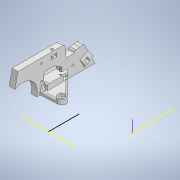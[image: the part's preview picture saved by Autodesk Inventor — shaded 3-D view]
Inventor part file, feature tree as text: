
AUTODESK INVENTOR PART (.ipt)
format: ipt  version: 2022.3 (Build 263350000, 350)  size: 2,605,056 bytes
history: native  units: mm
features: projected_geometry x116, extrude x97, sketch x67, fillet x9, reference x5, other x5, plane x4, mirror x3
ambient origin geometry x8: Origin, YZ Plane, XZ Plane, XY Plane, X Axis, Y Axis, Z Axis, Center Point
bodies: Solid1 (feature_tree)
feature tree (306):
  sketch  "Sketch1"  dims[d0=100.0mm d1=100.0mm]
  extrude  "Extrusion1"  Depth=100.0mm
  extrude  "Extrusion2"  Depth=20.0mm
  extrude  "Extrusion3"  Depth=20.0mm
  sketch  "Sketch3"  dims[d4=31.0mm d5=20.0mm]
  extrude  "Extrusion4"  Depth=19.0mm
  extrude  "Extrusion5"  Depth=10.0mm
  sketch  "Sketch4"  dims[d6=14.0mm d7=19.0mm]
  plane  "Work Plane1"
  mirror  "Mirror1"
  extrude  "Extrusion6"  Depth=2.0mm
  sketch  "Sketch8"  dims[d10=10.0mm d11=2.0mm]
  extrude  "Extrusion7"  Depth=15.0mm
  extrude  "Extrusion8"  Depth=2.0mm
  extrude  "Extrusion9"  Depth=5.0mm
  sketch  "Sketch9"  dims[d12=2.0mm d13=15.0mm]
  extrude  "Extrusion10"  Depth=2.0mm TaperAngle=0.0deg
  extrude  "Extrusion11"  TaperAngle=0.0deg  [1 undecoded]
  sketch  "Sketch10"  dims[d14=15.0mm d15=2.0mm]
  extrude  "Extrusion12"  Depth=14.0mm TaperAngle=0.0deg
  extrude  "Extrusion13"  TaperAngle=90.0deg  [1 undecoded]
  extrude  "Extrusion14"  Depth=40.0mm
  sketch  "Sketch12"  dims[d18=10.0mm d19=0.0mm d20=2.0mm d21=0.0mm]
  extrude  "Extrusion15"  Depth=15.0mm
  extrude  "Extrusion16"  Depth=5.0mm
  extrude  "Extrusion17"  Depth=13.0mm
  extrude  "Extrusion18"  Depth=8.0mm
  extrude  "Extrusion19"  Depth=18.0mm TaperAngle=0.0deg
  extrude  "Extrusion20"  Depth=49.0mm
  extrude  "Extrusion21"  Depth=5.0mm
  sketch  "Sketch15"  dims[d28=14.25mm d29=0.0mm d30=90.0deg]
  plane  "Work Plane2"
  mirror  "Mirror2"
  extrude  "Extrusion22"  TaperAngle=0.0deg  [1 undecoded]
  sketch  "Sketch17"  dims[d36=15.0mm d37=25.0mm]
  extrude  "Extrusion23"  Depth=10.0mm
  extrude  "Extrusion24"  Depth=1.6mm
  extrude  "Extrusion25"  TaperAngle=0.0deg  [1 undecoded]
  extrude  "Extrusion26"  Depth=14.0mm TaperAngle=0.0deg
  extrude  "Extrusion27"  Depth=2.0mm
  sketch  "Sketch21"  dims[d44=18.0mm d45=0.0mm d46=18.0mm d47=0.0mm]
  extrude  "Extrusion28"  Depth=2.0mm
  extrude  "Extrusion29"  Depth=6.0mm TaperAngle=0.0deg
  sketch  "Sketch22"  dims[d48=0.0mm d49=0.0mm d50=49.0mm]
  extrude  "Extrusion30"  Depth=15.0mm TaperAngle=0.0deg
  extrude  "Extrusion31"  Depth=15.0mm
  extrude  "Extrusion32"  Depth=4.0mm
  extrude  "Extrusion33"  Depth=15.0mm TaperAngle=0.0deg
  extrude  "Extrusion34"  Depth=3.0mm
  extrude  "Extrusion35"  Depth=15.0mm TaperAngle=0.0deg
  extrude  "Extrusion36"  Depth=3.2mm
  fillet  "Face Fillet1"
  fillet  "Face Fillet2"
  extrude  "Extrusion37"  Depth=3.2mm
  fillet  "Face Fillet3"
  fillet  "Face Fillet5"
  extrude  "Extrusion38"  Depth=5.0mm TaperAngle=0.0deg
  extrude  "Extrusion39"  TaperAngle=0.0deg  [1 undecoded]
  fillet  "Fillet2"  Radius=2.8mm
  extrude  "Extrusion40"  Depth=100.0mm TaperAngle=0.0deg
  sketch  "Sketch32"  dims[d76=6.0mm d77=0.0mm d78=15.0mm d79=0.0mm]
  extrude  "Extrusion41"  Depth=11.0mm
  extrude  "Extrusion42"  Depth=9.0mm TaperAngle=0.0deg
  extrude  "Extrusion43"  Depth=15.0mm
  sketch  "Sketch33"  dims[d80=15.0mm d81=0.0mm d82=3.2mm]
  extrude  "Extrusion44"  Depth=7.0mm TaperAngle=0.0deg
  extrude  "Extrusion45"  Depth=40.656mm TaperAngle=0.0deg
  extrude  "Extrusion46"  Depth=9.0mm TaperAngle=0.0deg
  extrude  "Extrusion47"  Depth=3.0mm
  sketch  "Sketch36"  dims[d91=90.0deg d92=3.0mm]
  extrude  "Extrusion48"  Depth=1.5mm TaperAngle=0.0deg
  extrude  "Extrusion49"  Depth=6.0mm
  sketch  "Sketch37"  dims[d93=3.0mm d94=15.0mm d95=0.0mm]
  extrude  "Extrusion50"  Depth=10.0mm TaperAngle=0.0deg
  extrude  "Extrusion51"  Depth=4.0mm
  extrude  "Extrusion52"  Depth=10.0mm TaperAngle=0.0deg
  extrude  "Extrusion53"  Depth=20.0mm TaperAngle=0.0deg
  sketch  "Sketch40"  dims[d100=4.0mm d101=5.0mm d102=0.0mm]
  extrude  "Extrusion54"  Depth=1.5mm
  extrude  "Extrusion55"  Depth=3.0mm
  extrude  "Extrusion56"  Depth=6.4mm
  extrude  "Extrusion57"  Depth=2.0mm
  fillet  "Fillet3"  Radius=2.0mm
  extrude  "Extrusion58"  TaperAngle=0.0deg  [1 undecoded]
  sketch  "Sketch44"  dims[d114=3.4mm d115=9.0mm d116=0.0mm]
  extrude  "Extrusion59"  TaperAngle=0.0deg  [1 undecoded]
  extrude  "Extrusion60"  Depth=10.0mm TaperAngle=0.0deg
  sketch  "Sketch45"  dims[d117=15.0mm d118=0.0mm d119=3.2mm]
  extrude  "Extrusion61"  Depth=10.0mm TaperAngle=0.0deg
  extrude  "Extrusion62"  Depth=2.0mm
  sketch  "Sketch46"  dims[d120=3.2mm d121=7.0mm d122=0.0mm]
  extrude  "Extrusion63"  Depth=6.5mm TaperAngle=0.0deg
  extrude  "Extrusion64"  Depth=17.0mm TaperAngle=0.0deg
  extrude  "Extrusion65"  Depth=3.0mm
  extrude  "Extrusion66"  Depth=5.0mm TaperAngle=0.0deg
  sketch  "Sketch49"  dims[d138=28.734mm d139=3.0mm]
  extrude  "Extrusion67"  Depth=15.0mm TaperAngle=0.0deg
  extrude  "Extrusion68"  TaperAngle=0.0deg  [1 undecoded]
  extrude  "Extrusion69"  Depth=15.0mm TaperAngle=0.0deg
  extrude  "Extrusion70"  Depth=15.0mm TaperAngle=0.0deg
  extrude  "Extrusion71"  Depth=2.0mm
  extrude  "Extrusion72"  Depth=15.0mm TaperAngle=0.0deg
  extrude  "Extrusion73"  Depth=15.0mm TaperAngle=0.0deg
  extrude  "Extrusion74"  Depth=15.0mm TaperAngle=0.0deg
  extrude  "Extrusion75"  Depth=15.0mm TaperAngle=0.0deg
  extrude  "Extrusion76"  Depth=15.0mm TaperAngle=0.0deg
  sketch  "Sketch53"  dims[d149=6.7mm d152=4.0mm]
  extrude  "Extrusion77"  Depth=15.0mm
  extrude  "Extrusion78"  Depth=15.0mm
  extrude  "Extrusion79"  Depth=2.0mm
  extrude  "Extrusion80"  Depth=15.0mm
  extrude  "Extrusion81"  TaperAngle=0.0deg  [1 undecoded]
  extrude  "Extrusion82"  Depth=15.0mm TaperAngle=0.0deg
  extrude  "Extrusion83"  Depth=15.0mm TaperAngle=0.0deg
  sketch  "Sketch59"  dims[d166=6.4mm d167=3.0mm d169=2.0mm]
  extrude  "Extrusion84"  Depth=15.0mm
  extrude  "Extrusion85"  Depth=15.0mm
  extrude  "Extrusion86"  Depth=15.0mm TaperAngle=0.0deg
  extrude  "Extrusion87"  Depth=15.0mm
  extrude  "Extrusion88"  Depth=2.0mm
  sketch  "Sketch62"  dims[d178=10.0mm d179=0.0mm d180=4.0mm d181=0.0mm]
  extrude  "Extrusion89"  Depth=15.0mm
  extrude  "Extrusion90"  Depth=15.0mm
  fillet  "Fillet4"  Radius=15.0mm
  extrude  "Extrusion91"  Depth=10.0mm TaperAngle=0.0deg
  mirror  "Mirror3"
  extrude  "Extrusion92"  Depth=10.0mm TaperAngle=0.0deg
  extrude  "Extrusion93"  Depth=15.0mm TaperAngle=0.0deg
  fillet  "Fillet5"  Radius=10.0mm
  extrude  "Extrusion94"  Depth=15.0mm TaperAngle=0.0deg
  fillet  "Fillet6"  Radius=4.0mm
  extrude  "Extrusion95"  Depth=15.0mm
  extrude  "Extrusion96"  Depth=10.0mm TaperAngle=0.0deg
  extrude  "Extrusion97"  Depth=15.0mm
  sketch  "Sketch2"  dims[d2=5.0mm d3=20.0mm]
  projected_geometry  "Projected Loop1"
  sketch  "Sketch6"  dims[d8=10.0mm d9=14.0mm]
  projected_geometry  "Projected Loop5"
  projected_geometry  "Projected Loop6"
  projected_geometry  "Projected Loop7"
  projected_geometry  "Projected Loop8"
  projected_geometry  "Projected Loop9"
  projected_geometry  "Projected Loop10"
  sketch  "Sketch11"  dims[d16=1.0mm d17=5.0mm]
  projected_geometry  "Projected Loop11"
  projected_geometry  "Projected Loop12"
  sketch  "Sketch13"  dims[d22=31.0mm d23=0.0mm d24=0.0mm]
  projected_geometry  "Projected Loop13"
  projected_geometry  "Projected Loop14"
  sketch  "Sketch14"  dims[d25=30.4mm d26=14.0mm d27=0.0mm]
  projected_geometry  "Projected Loop15"
  projected_geometry  "Projected Loop16"
  sketch  "Sketch16"  dims[d33=25.0mm d34=0.0mm d35=40.0mm]
  projected_geometry  "Projected Loop17"
  projected_geometry  "Projected Loop18"
  projected_geometry  "Projected Loop19"
  sketch  "Sketch18"  dims[d38=20.0mm d39=5.0mm]
  projected_geometry  "Projected Loop20"
  projected_geometry  "Projected Loop21"
  projected_geometry  "Projected Loop22"
  projected_geometry  "Projected Loop23"
  projected_geometry  "Projected Loop24"
  projected_geometry  "Projected Loop25"
  projected_geometry  "Projected Loop26"
  sketch  "Sketch19"  dims[d40=7.0mm d41=13.0mm]
  projected_geometry  "Projected Loop27"
  sketch  "Sketch20"  dims[d42=7.0mm d43=8.0mm]
  projected_geometry  "Projected Loop28"
  projected_geometry  "Projected Loop29"
  projected_geometry  "Projected Loop30"
  sketch  "Sketch23"  dims[d51=25.0mm d52=5.0mm]
  sketch  "Sketch24"  dims[d53=20.0mm d54=0.0mm d55=0.0mm]
  projected_geometry  "Projected Loop31"
  projected_geometry  "Projected Loop32"
  sketch  "Sketch25"  dims[d56=10.0mm d57=0.0mm d58=1.6mm]
  projected_geometry  "Projected Loop33"
  sketch  "Sketch26"  dims[d59=1.6mm d60=1.6mm]
  projected_geometry  "Projected Loop34"
  sketch  "Sketch27"  dims[d61=5.0mm d62=0.0mm d63=0.0mm d64=0.0mm]
  projected_geometry  "Projected Loop35"
  sketch  "Sketch28"  dims[d65=2.5mm d66=14.0mm d67=0.0mm]
  projected_geometry  "Projected Loop36"
  sketch  "Sketch29"  dims[d68=2.0mm d69=6.0mm]
  sketch  "Sketch30"  dims[d70=5.0mm d71=2.0mm]
  projected_geometry  "Projected Loop37"
  projected_geometry  "Projected Loop38"
  projected_geometry  "Projected Loop39"
  sketch  "Sketch31"  dims[d72=14.0mm d73=0.0mm d74=6.0mm d75=0.0mm]
  projected_geometry  "Projected Loop40"
  projected_geometry  "Projected Loop41"
  projected_geometry  "Projected Loop42"
  projected_geometry  "Projected Loop43"
  projected_geometry  "Projected Loop44"
  projected_geometry  "Projected Loop45"
  projected_geometry  "Projected Loop46"
  sketch  "Sketch34"  dims[d83=3.2mm d84=4.0mm]
  projected_geometry  "Projected Loop47"
  projected_geometry  "Projected Loop48"
  sketch  "Sketch35"  dims[d85=15.0mm d86=0.0mm d87=1.0mm d88=0.0mm]
  projected_geometry  "Projected Loop49"
  projected_geometry  "Projected Loop50"
  projected_geometry  "Projected Loop51"
  projected_geometry  "Projected Loop52"
  projected_geometry  "Projected Loop53"
  sketch  "Sketch38"  dims[d96=3.2mm d97=3.2mm]
  projected_geometry  "Projected Loop54"
  projected_geometry  "Projected Loop55"
  sketch  "Sketch39"  dims[d98=3.2mm d99=3.2mm]
  projected_geometry  "Projected Loop56"
  sketch  "Sketch41"  dims[d103=5.0mm d104=0.0mm d105=0.0mm d106=0.0mm d107=2.8mm]
  projected_geometry  "Projected Loop57"
  sketch  "Sketch42"  dims[d108=2.8mm d109=100.0mm d110=0.0mm]
  projected_geometry  "Projected Loop58"
  sketch  "Sketch43"  dims[d111=20.0mm d112=0.0mm d113=11.0mm]
  projected_geometry  "Projected Loop59"
  projected_geometry  "Projected Loop60"
  projected_geometry  "Projected Loop61"
  projected_geometry  "Projected Loop62"
  projected_geometry  "Projected Loop63"
  projected_geometry  "Projected Loop64"
  projected_geometry  "Projected Loop65"
  projected_geometry  "Projected Loop66"
  projected_geometry  "Projected Loop67"
  projected_geometry  "Projected Loop68"
  projected_geometry  "Projected Loop69"
  projected_geometry  "Projected Loop70"
  projected_geometry  "Projected Loop71"
  projected_geometry  "Projected Loop72"
  projected_geometry  "Projected Loop73"
  projected_geometry  "Projected Loop74"
  projected_geometry  "Projected Loop75"
  projected_geometry  "Projected Loop76"
  projected_geometry  "Projected Loop77"
  projected_geometry  "Projected Loop78"
  sketch  "Sketch47"  dims[d123=4.0mm d124=0.0mm d125=40.656mm d126=0.0mm]
  projected_geometry  "Projected Loop79"
  sketch  "Sketch48"  dims[d127=3.0mm d128=0.0mm d129=9.0mm d130=0.0mm]
  projected_geometry  "Projected Loop80"
  projected_geometry  "Projected Loop81"
  sketch  "Sketch50"  dims[d140=1.5mm d141=0.0mm d142=1.5mm d143=0.0mm]
  projected_geometry  "Projected Loop82"
  projected_geometry  "Projected Loop83"
  sketch  "Sketch51"  dims[d144=6.0mm d145=6.0mm]
  projected_geometry  "Projected Loop84"
  sketch  "Sketch52"  dims[d146=2.0mm d147=10.0mm d148=0.0mm]
  projected_geometry  "Projected Loop85"
  projected_geometry  "Projected Loop86"
  projected_geometry  "Projected Loop87"
  sketch  "Sketch54"  dims[d153=10.0mm d154=0.0mm d155=16.0mm d156=0.0mm]
  projected_geometry  "Projected Loop88"
  projected_geometry  "Projected Loop89"
  sketch  "Sketch55"  dims[d157=1e-05mm d158=20.0mm d159=0.0mm]
  projected_geometry  "Projected Loop90"
  projected_geometry  "Projected Loop91"
  sketch  "Sketch56"  dims[d160=6.4mm d161=1.5mm]
  projected_geometry  "Projected Loop92"
  projected_geometry  "Projected Loop93"
  projected_geometry  "Projected Loop94"
  sketch  "Sketch57"  dims[d162=16.5mm d163=3.0mm]
  projected_geometry  "Projected Loop95"
  projected_geometry  "Projected Loop96"
  projected_geometry  "Projected Loop97"
  sketch  "Sketch58"  dims[d164=3.0mm d165=6.4mm]
  projected_geometry  "Projected Loop98"
  projected_geometry  "Projected Loop99"
  projected_geometry  "Projected Loop100"
  projected_geometry  "Projected Loop101"
  sketch  "Sketch60"  dims[d170=5.928mm d171=0.0mm d172=0.0mm d173=0.0mm]
  projected_geometry  "Projected Loop102"
  projected_geometry  "Projected Loop103"
  sketch  "Sketch61"  dims[d174=3.0mm d175=0.0mm d176=0.0mm d177=0.0mm]
  projected_geometry  "Projected Loop104"
  projected_geometry  "Projected Loop105"
  projected_geometry  "Projected Loop106"
  projected_geometry  "Projected Loop107"
  projected_geometry  "Projected Loop108"
  projected_geometry  "Projected Loop109"
  projected_geometry  "Projected Loop110"
  projected_geometry  "Projected Loop111"
  sketch  "Sketch63"  dims[d182=2.5mm d183=10.0mm d184=0.0mm]
  projected_geometry  "Projected Loop112"
  plane  "Work Plane3"
  plane  "Work Plane4"
  sketch  "Sketch64"  dims[d185=2.0mm d186=3.0mm]
  projected_geometry  "Projected Loop113"
  sketch  "Sketch65"  dims[d195=0.0mm d196=0.0mm d197=6.5mm d198=0.0mm]
  projected_geometry  "Projected Loop114"
  sketch  "Sketch66"  dims[d199=2.5mm d200=17.0mm d201=0.0mm]
  projected_geometry  "Projected Loop115"
  projected_geometry  "Projected Loop116"
  sketch  "Sketch67"  dims[d202=14.0mm d203=0.0mm d204=3.0mm]
  reference  "Reference1"
  reference  "Reference2"
  reference  "Reference3"
  projected_geometry  "Projected Loop117"
  reference  "Reference4"
  sketch  "Sketch68"  dims[d205=4.0mm d206=0.0mm d207=5.0mm d208=0.0mm]
  reference  "Reference5"
  projected_geometry  "Projected Loop118"
  sketch  "Sketch69"  dims[d209=2.5mm d210=6.5mm d211=0.0mm d212=0.0mm d213=0.0mm d214=14.0mm d215=0.0mm d216=6.5mm d217=0.0mm d218=2.0mm d219=6.5mm d220=0.0mm d221=16.0mm d222=0.0mm d223=17.0mm d224=0.0mm d225=17.0mm d226=0.0mm d227=17.0mm d228=0.0mm d229=2.5mm d230=2.5mm d231=2.0mm d232=13.0mm d233=0.0mm d234=0.0mm d235=6.5mm d236=0.0mm d237=3.0mm d238=0.0mm d239=1.0mm d240=2.5mm d241=14.0mm d242=0.0mm d243=1.0mm d244=2.0mm d245=3.0mm d246=3.2mm d247=15.0mm d248=0.0mm d249=10.0mm d250=0.0mm d251=10.0mm d252=0.0mm d253=3.0mm d254=0.0mm d255=10.0mm d256=0.0mm d257=8.0mm d258=0.0mm d259=4.0mm d260=0.0mm d261=2.5mm d262=10.0mm d263=0.0mm d266=7.0mm d268=7.0mm d269=6.5mm d270=0.0mm d271=3.0mm d272=0.0mm d273=8.0mm d274=0.0mm d275=4.0mm d276=0.0mm d277=1.0mm d278=1.0mm d279=10.0mm d280=0.0mm d281=1.308997mm d282=45.0mm d283=30.0mm d284=0.0mm d285=2.0mm d286=2.5mm d287=11.0mm d288=0.0mm d289=135.0deg d290=0.0mm d291=0.0mm d292=3.7mm d293=0.0mm d294=10.0mm d295=6.4mm d296=3.0mm d297=0.0mm d298=0.0mm d299=1.0mm d300=0.0mm d301=1.5mm d302=0.0mm d303=5.928mm d304=0.0mm d305=12.0mm d306=0.0mm d307=12.0mm d308=0.0mm d309=12.0mm d310=0.0mm d311=2.0mm d312=41.5mm d313=0.0mm d314=10.0mm d315=0.0mm d316=20.0mm d317=10.0mm d318=10.0mm d319=0.0mm d320=2.0mm d321=4.0mm d322=0.0mm d323=2.0mm d324=45.02mm d325=22.51mm d326=6.5mm d327=0.0mm d328=6.5mm d329=0.0mm d330=2.5mm d331=15.0mm d332=0.0mm d150=0.0mm d151=0.0mm]
  projected_geometry  "Projected Loop119"
  other  "Assembly2"
  other  "koło_minisumo:1"
  other  "minisumopodsr:1"
  other  "uchwytlewy:1"
  other  "pokrywa:1"
note: 9 required parameter values undecoded (feature->parameter linkage not recoverable at this tier; creation-order binding heuristic only, values carry confidence <= 0.55)
